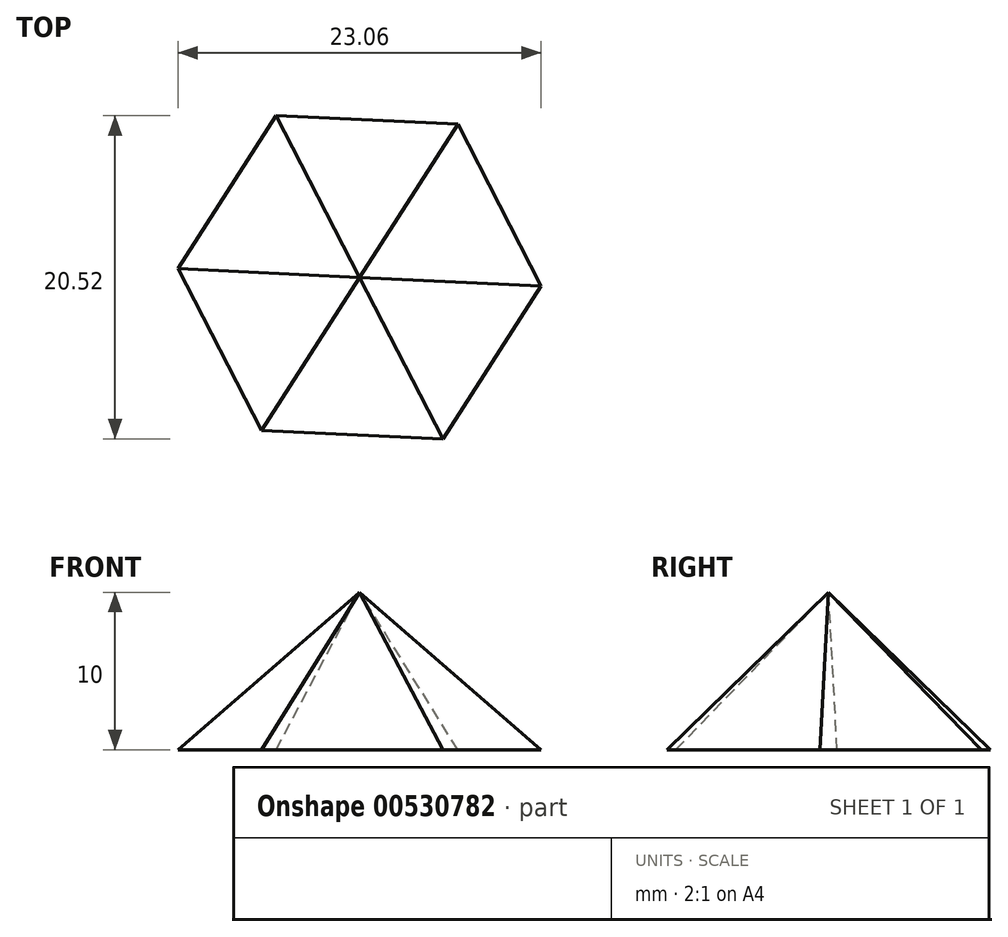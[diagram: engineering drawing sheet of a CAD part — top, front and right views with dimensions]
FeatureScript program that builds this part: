
annotation { "Feature Type Name" : "Feature", "Feature Type Description" : "" }
export const myFeature = defineFeature(function(context is Context, id is Id, definition is map)
    precondition{}
    {
        {
            var Q0;
            Q0=qCreatedBy(makeId("Top.planeOp"),FACE);
            var sketch = newSketch(context, id + "F0", { "sketchPlane" : qUnion([Q0])});
            skCircle(sketch, "E0.cCircle", {"center": v(0, 0) * mm, "radius": 10 * mm, "construction": true});
            skLineSegment(sketch, "E0.0", {"start": v(-11.53, 0.54) * mm, "end": v(-5.3, 10.26) * mm});
            skLineSegment(sketch, "E0.1", {"start": v(-5.3, 10.26) * mm, "end": v(6.24, 9.72) * mm});
            skLineSegment(sketch, "E0.2", {"start": v(6.24, 9.72) * mm, "end": v(11.53, -0.54) * mm});
            skLineSegment(sketch, "E0.3", {"start": v(11.53, -0.54) * mm, "end": v(5.3, -10.26) * mm});
            skLineSegment(sketch, "E0.4", {"start": v(5.3, -10.26) * mm, "end": v(-6.24, -9.72) * mm});
            skLineSegment(sketch, "E0.5", {"start": v(-6.24, -9.72) * mm, "end": v(-11.53, 0.54) * mm});
            skPoint(sketch, "E0.0.midPoint", {"position": v(-8.42, 5.4) * mm});
            skSolve(sketch);
        }
        {
            var Q0;
            Q0 = qSketchRegion(id + "F7jGFYteNnkNGyh_1", true);
            var Q1;
            Q1=qCreatedBy(makeId("Top.planeOp"),FACE);
            cPlane(context, id + "F1", {"entities" : qUnion([Q0, Q1]), "cplaneType" : CPlaneType.OFFSET, "offset" : 10 * mm, "width" : 150 * mm, "height" : 150 * mm});
        }
        {
            var Q0;
            Q0=qCreatedBy(id+"F1.planeOp",FACE);
            var sketch = newSketch(context, id + "F2", { "sketchPlane" : qUnion([Q0])});
            skPoint(sketch, "E1", {"position": v(0, 0) * mm});
            skSolve(sketch);
        }
        {
            var Q0;
            Q0=makeQuery(id+"F0.imprint","IMPRINT",FACE,{"disambiguationData":[TD([[makeQuery(id+"F0.imprint","IMPRINT",EDGE,{"derivedFrom":sQuery(id+"F0.wireOp",EDGE,"E0.0")}),-1.0]])]});
            var Q1;
            Q1=sQuery(id+"F2.wireOp",VERTEX,"E1");
            loft(context, id + "F3", {"sheetProfilesArray" : [{ "sheetProfileEntities" : qUnion([Q0]) }, { "sheetProfileEntities" : qUnion([Q1]) }]});
        }
    });
